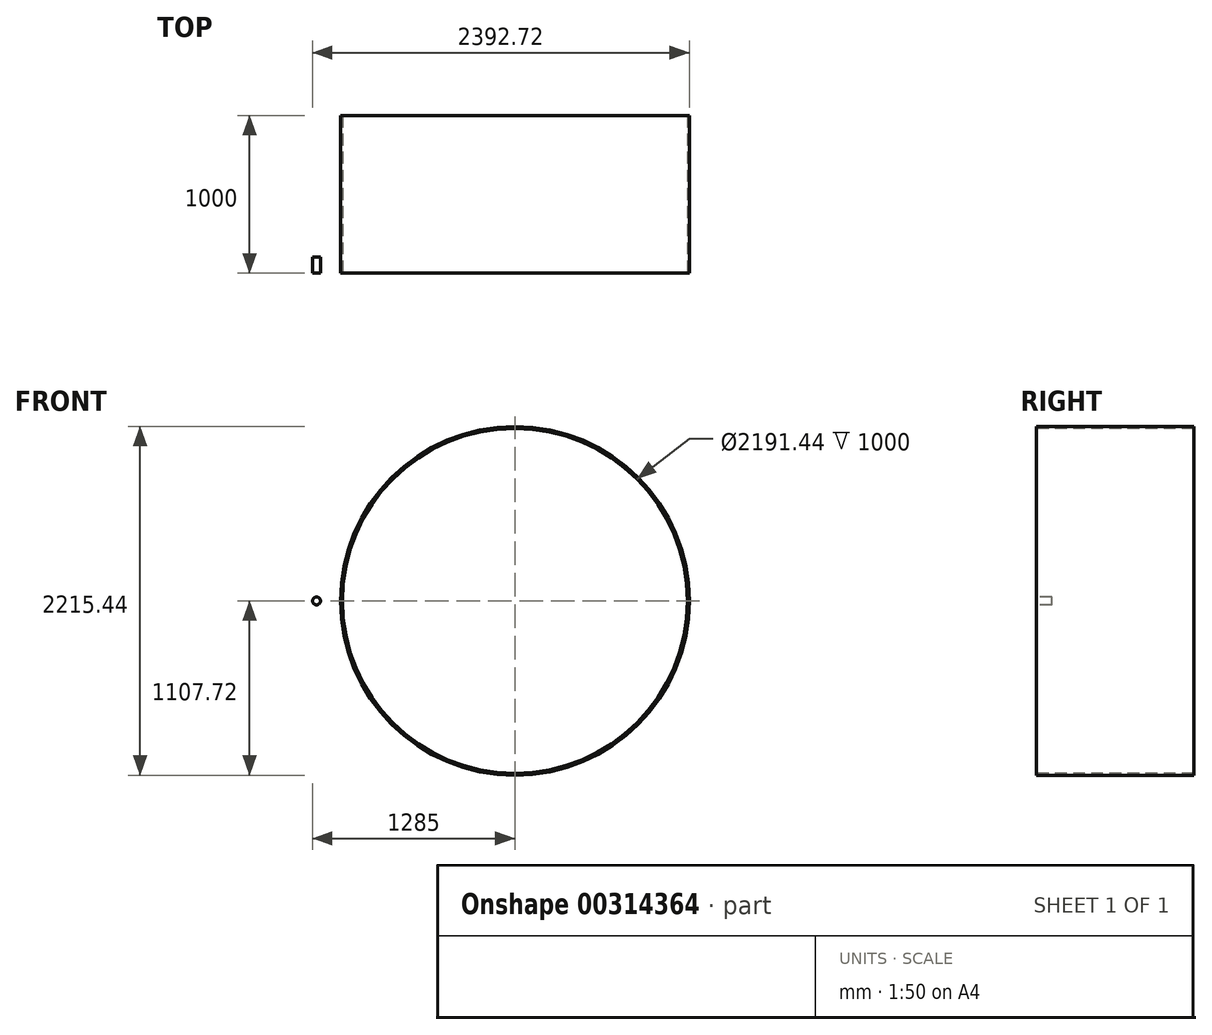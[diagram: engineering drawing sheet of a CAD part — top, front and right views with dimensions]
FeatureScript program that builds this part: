
annotation { "Feature Type Name" : "Feature", "Feature Type Description" : "" }
export const myFeature = defineFeature(function(context is Context, id is Id, definition is map)
    precondition{}
    {
        {
            var Q0;
            Q0=qCreatedBy(makeId("Front.planeOp"),FACE);
            var sketch = newSketch(context, id + "F0", { "sketchPlane" : qUnion([Q0])});
            skCircle(sketch, "E0", {"center": v(0, 0) * mm, "radius": 25 * mm});
            skSolve(sketch);
        }
        {
            var Q0;
            Q0=makeQuery(id+"F0.imprint","IMPRINT",FACE,{"disambiguationData":[TD([[makeQuery(id+"F0.imprint","IMPRINT",EDGE,{"derivedFrom":sQuery(id+"F0.wireOp",EDGE,"E0")}),1.0]])]});
            extrude(context, id + "F1", {"entities" : qUnion([Q0]), "oppositeDirection" : true, "depth" : 100 * mm});
        }
        {
            var Q0;
            Q0=qCreatedBy(makeId("Front.planeOp"),FACE);
            var sketch = newSketch(context, id + "F2", { "sketchPlane" : qUnion([Q0])});
            skCircle(sketch, "E1", {"center": v(1260, 0) * mm, "radius": 1107.72 * mm});
            skCircle(sketch, "E2", {"center": v(1260, 0) * mm, "radius": 1095.72 * mm});
            skSolve(sketch);
        }
        {
            var Q0;
            Q0=makeQuery(id+"F2.imprint","IMPRINT",FACE,{"disambiguationData":[TD([[makeQuery(id+"F2.imprint","IMPRINT",EDGE,{"derivedFrom":sQuery(id+"F2.wireOp",EDGE,"E1")}),1.0]])]});
            extrude(context, id + "F3", {"entities" : qUnion([Q0]), "oppositeDirection" : true, "depth" : 1000 * mm});
        }
    });
